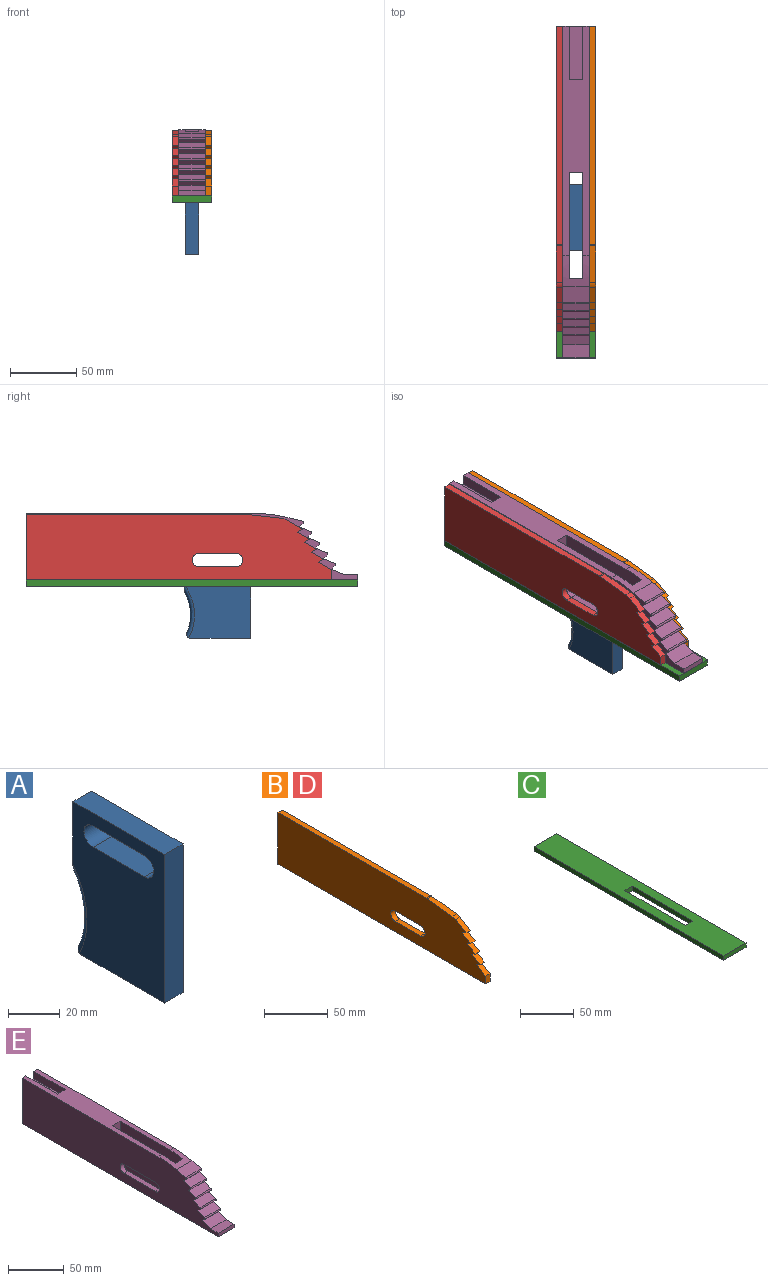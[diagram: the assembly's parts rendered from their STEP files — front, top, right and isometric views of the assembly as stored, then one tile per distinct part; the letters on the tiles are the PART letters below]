
ASSEMBLY  parts=5 mates=13
PART A: 15 faces, bbox 10.1x52.5x72.3 mm
  f0: cylinder r=5mm len=10mm, axis (-1,0,0), area 157.1mm2, adj f1,f8,f9,f10
  f1: plane 28x10mm, normal (0,0,-1), area 280mm2, adj f0,f2,f9,f10
  f2: cylinder r=5mm len=10mm, axis (-1,0,0), area 157.1mm2, adj f1,f8,f9,f10
  f3: plane 70x10mm, normal (0,-1,0), area 700mm2, adj f4,f7,f9,f10
  f4: plane 45.19x10mm, normal (0,0,-1), area 451.9mm2, adj f3,f9,f10,f11
  f5: cylinder r=35mm len=29.8mm, axis (-1,0,0), area 123.3mm2, adj f11,f12,f13,f14
  f6: plane 33.83x10.12mm, normal (0,1,0), area 334.2mm2, adj f7,f9,f10,f12,f13,f14
  f7: plane 50x10mm, normal (0,0,1), area 500mm2, adj f3,f6,f9,f10
  f8: plane 28x10mm, normal (0,0,1), area 280mm2, adj f0,f2,f9,f10
  f9: plane 70x50mm, normal (1,0,0), area 2911mm2, adj f0,f1,f2,f3,f4,f6,f7,f8
  f10: plane 70x50mm, normal (-1,0,0), area 2911mm2, adj f0,f1,f2,f3,f4,f6,f7,f8
  f11: cylinder r=3mm len=10mm, axis (-1,0,0), area 49mm2, adj f4,f5,f9,f10,f13,f14
  f12: cylinder r=5mm len=7.76mm, axis (-1,0,0), area 14.4mm2, adj f5,f6,f13,f14
  f13: torus R=38mm, axis (1,0,0), area 172mm2, adj f5,f6,f9,f11,f12
  f14: torus R=38mm, axis (1,0,0), area 172mm2, adj f5,f6,f10,f11,f12
PART B: 22 faces, bbox 5x230x49.5 mm
  f0: plane 49.5x5mm, normal (0,1,0), area 247.5mm2, adj f1,f12,f13,f15
  f1: plane 164.4x5mm, normal (0,0,1), area 822mm2, adj f0,f12,f13,f16
  f2: plane 27.28x5mm, normal (0,-0.11,0.99), area 137.3mm2, adj f12,f13,f16,f17
  f3: plane 11.47x6.88mm, normal (0,-0.51,0.86), area 66.9mm2, adj f4,f12,f13,f17
  f4: plane 5x4mm, normal (0,-0.45,-0.89), area 22.4mm2, adj f3,f5,f12,f13
  f5: plane 9.24x5.54mm, normal (0,-0.51,0.86), area 53.9mm2, adj f4,f6,f12,f13
  f6: plane 5x4mm, normal (0,-0.45,-0.89), area 22.4mm2, adj f5,f7,f12,f13
  f7: plane 9.24x5.54mm, normal (0,-0.51,0.86), area 53.9mm2, adj f6,f8,f12,f13
  f8: plane 5x4mm, normal (0,-0.45,-0.89), area 22.4mm2, adj f7,f9,f12,f13
  f9: plane 9.24x5.54mm, normal (0,-0.51,0.86), area 53.9mm2, adj f8,f10,f12,f13
  f10: plane 5x4mm, normal (0,-0.45,-0.89), area 22.4mm2, adj f9,f11,f12,f13
  f11: plane 10x6mm, normal (0,-0.51,0.86), area 58.3mm2, adj f10,f12,f13,f14
  f12: plane 230x49.5mm, normal (1,0,0), area 10209.8mm2, adj f0,f1,f2,f3,f4,f5,f6,f7
  f13: plane 230x49.5mm, normal (-1,0,0), area 10209.8mm2, adj f0,f1,f2,f3,f4,f5,f6,f7
  f14: plane 7.5x5mm, normal (0,-1,0), area 37.5mm2, adj f11,f12,f13,f15
  f15: plane 230x5mm, normal (0,0,-1), area 1150mm2, adj f0,f12,f13,f14
  f16: cylinder r=10mm len=5mm, axis (1,0,0), area 5.6mm2, adj f1,f2,f12,f13
  f17: cylinder r=10mm len=5mm, axis (-1,0,0), area 21.4mm2, adj f2,f3,f12,f13
  f18: cylinder r=5mm len=10mm, axis (1,0,0), area 78.5mm2, adj f12,f13,f19,f21
  f19: plane 28x5mm, normal (0,0,1), area 140mm2, adj f12,f13,f18,f20
  f20: cylinder r=5mm len=10mm, axis (1,0,0), area 78.5mm2, adj f12,f13,f19,f21
  f21: plane 28x5mm, normal (0,0,-1), area 140mm2, adj f12,f13,f18,f20
PART C: 10 faces, bbox 30x250x5 mm
  f0: plane 250x30mm, normal (0,0,1), area 6700mm2, adj f2,f3,f4,f5,f6,f7,f8,f9
  f1: plane 250x30mm, normal (0,0,-1), area 6700mm2, adj f2,f3,f4,f5,f6,f7,f8,f9
  f2: plane 30x5mm, normal (0,-1,0), area 150mm2, adj f0,f1,f3,f5
  f3: plane 250x5mm, normal (1,0,0), area 1250mm2, adj f0,f1,f2,f4
  f4: plane 30x5mm, normal (0,1,0), area 150mm2, adj f0,f1,f3,f5
  f5: plane 250x5mm, normal (-1,0,0), area 1250mm2, adj f0,f1,f2,f4
  f6: plane 80x5mm, normal (-1,0,0), area 400mm2, adj f0,f1,f7,f8
  f7: plane 10x5mm, normal (0,-1,0), area 50mm2, adj f0,f1,f6,f9
  f8: plane 10x5mm, normal (0,1,0), area 50mm2, adj f0,f1,f6,f9
  f9: plane 80x5mm, normal (1,0,0), area 400mm2, adj f0,f1,f7,f8
PART D: same geometry as B
PART E: 40 faces, bbox 20x250x50 mm
  f0: plane 173.17x20mm, normal (0,0,1), area 2431.7mm2, adj f7,f8,f9,f27,f32,f33,f34,f36
  f1: plane 40x5mm, normal (0,0,-1), area 200mm2, adj f2,f3,f8,f33
  f2: cylinder r=5mm len=10mm, axis (1,0,0), area 78.5mm2, adj f1,f4,f8,f33
  f3: cylinder r=5mm len=10mm, axis (1,0,0), area 78.5mm2, adj f1,f4,f8,f33
  f4: plane 40x5mm, normal (0,0,1), area 200mm2, adj f2,f3,f8,f33
  f5: plane 20x4mm, normal (0,-1,0), area 80mm2, adj f6,f8,f9,f12
  f6: plane 250x20mm, normal (0,0,-1), area 4200mm2, adj f5,f7,f8,f9,f32,f33,f34,f35
  f7: plane 50x20mm, normal (0,1,0), area 920mm2, adj f0,f6,f8,f9,f36,f37,f38
  f8: plane 250x50mm, normal (1,0,0), area 10558.1mm2, adj f0,f1,f2,f3,f4,f5,f6,f7
  f9: plane 250x50mm, normal (-1,0,0), area 10558.1mm2, adj f0,f5,f6,f7,f10,f11,f12,f13
  f10: plane 20x2.74mm, normal (0,-0.71,-0.71), area 77.4mm2, adj f8,f9,f21,f22
  f11: plane 20x11.76mm, normal (0,-0.23,0.97), area 241.8mm2, adj f8,f9,f22,f27
  f12: plane 20x10mm, normal (0,0,1), area 200mm2, adj f5,f8,f9,f13
  f13: plane 20x10mm, normal (0,-0.37,0.93), area 215.4mm2, adj f8,f9,f12,f14
  f14: plane 20x2.93mm, normal (0,-0.71,-0.71), area 82.8mm2, adj f8,f9,f13,f23
  f15: plane 20x8.59mm, normal (0,-0.37,0.93), area 185.1mm2, adj f8,f9,f16,f23
  f16: plane 20x2.93mm, normal (0,-0.71,-0.71), area 82.8mm2, adj f8,f9,f15,f24
  f17: plane 20x8.59mm, normal (0,-0.37,0.93), area 185.1mm2, adj f8,f9,f18,f24
  f18: plane 20x2.93mm, normal (0,-0.71,-0.71), area 82.8mm2, adj f8,f9,f17,f25
  f19: plane 20x8.59mm, normal (0,-0.37,0.93), area 185.1mm2, adj f8,f9,f20,f25
  f20: plane 20x2.93mm, normal (0,-0.71,-0.71), area 82.8mm2, adj f8,f9,f19,f26
  f21: plane 20x8.59mm, normal (0,-0.37,0.93), area 185.1mm2, adj f8,f9,f10,f26
  f22: cylinder r=1mm len=20mm, axis (1,0,0), area 42.4mm2, adj f8,f9,f10,f11
  f23: cylinder r=1mm len=20mm, axis (1,0,0), area 39.5mm2, adj f8,f9,f14,f15
  f24: cylinder r=1mm len=20mm, axis (1,0,0), area 39.5mm2, adj f8,f9,f16,f17
  f25: cylinder r=1mm len=20mm, axis (1,0,0), area 39.5mm2, adj f8,f9,f18,f19
  f26: cylinder r=1mm len=20mm, axis (1,0,0), area 39.5mm2, adj f8,f9,f20,f21
  f27: cylinder r=100mm len=23.34mm, axis (-1,0,0), area 302mm2, adj f0,f8,f9,f11,f32,f33,f35
  f28: plane 40x5mm, normal (0,0,-1), area 200mm2, adj f9,f29,f30,f32
  f29: cylinder r=5mm len=10mm, axis (1,0,0), area 78.5mm2, adj f9,f28,f31,f32
  f30: cylinder r=5mm len=10mm, axis (1,0,0), area 78.5mm2, adj f9,f28,f31,f32
  f31: plane 40x5mm, normal (0,0,1), area 200mm2, adj f9,f29,f30,f32
  f32: plane 80x50mm, normal (1,0,0), area 3513.5mm2, adj f0,f6,f27,f28,f29,f30,f31,f34
  f33: plane 80x50mm, normal (-1,0,0), area 3513.5mm2, adj f0,f1,f2,f3,f4,f6,f27,f34
  f34: plane 50x10mm, normal (0,-1,0), area 500mm2, adj f0,f6,f32,f33
  f35: plane 48.57x10mm, normal (0,1,0), area 485.7mm2, adj f6,f27,f32,f33
  f36: plane 40x8mm, normal (1,0,0), area 320mm2, adj f0,f7,f38,f39
  f37: plane 40x8mm, normal (-1,0,0), area 320mm2, adj f0,f7,f38,f39
  f38: plane 40x10mm, normal (0,0,1), area 400mm2, adj f7,f36,f37,f39
  f39: plane 10x8mm, normal (0,1,0), area 80mm2, adj f0,f36,f37,f38
PLACE A t=(33.89,28.17,139.08)mm
PLACE B t=(48.89,-143.09,1.65)mm
PLACE C t=(140.84,-112.46,80.8)mm
PLACE D t=(23.89,-143.09,1.65)mm
PLACE E t=(28.89,-145.76,85.8)mm
MATE planar A.f9 <-> E.f33  axis (1,0,0) through (43.89,-41.67,75.16)mm
MATE parallel B.f13 <-> E.f8  axis (-1,0,0) through (48.89,21.86,135.3)mm
MATE planar C.f2 <-> E.f5  axis (0,-1,0) through (38.89,-145.76,83.3)mm
MATE planar C.f3 <-> B.f12  axis (1,0,0) through (53.89,-20.76,83.3)mm
MATE planar B.f13 <-> E.f8  axis (-1,0,0) through (48.89,-110.7,106.84)mm
MATE planar E.f6 <-> C.f0  axis (0,0,-1) through (38.89,-16,85.8)mm
MATE planar D.f12 <-> E.f9  axis (1,0,0) through (28.89,-1.82,110.02)mm
MATE planar D.f15 <-> E.f6  axis (0,0,-1) through (26.39,-10.94,85.8)mm
MATE cylindrical A.f2 <-> B.f20  axis (-1,0,0) through (38.89,-25.94,100.8)mm
MATE planar B.f15 <-> E.f6  axis (0,0,-1) through (51.39,-10.94,85.8)mm
MATE planar A.f8 <-> B.f19  axis (0,0,1) through (38.89,-39.94,95.8)mm
MATE parallel B.f15 <-> E.f6  axis (0,0,-1) through (51.39,-10.94,85.8)mm
MATE planar B.f0 <-> D.f0  axis (0,1,0) through (51.39,104.06,110.55)mm
